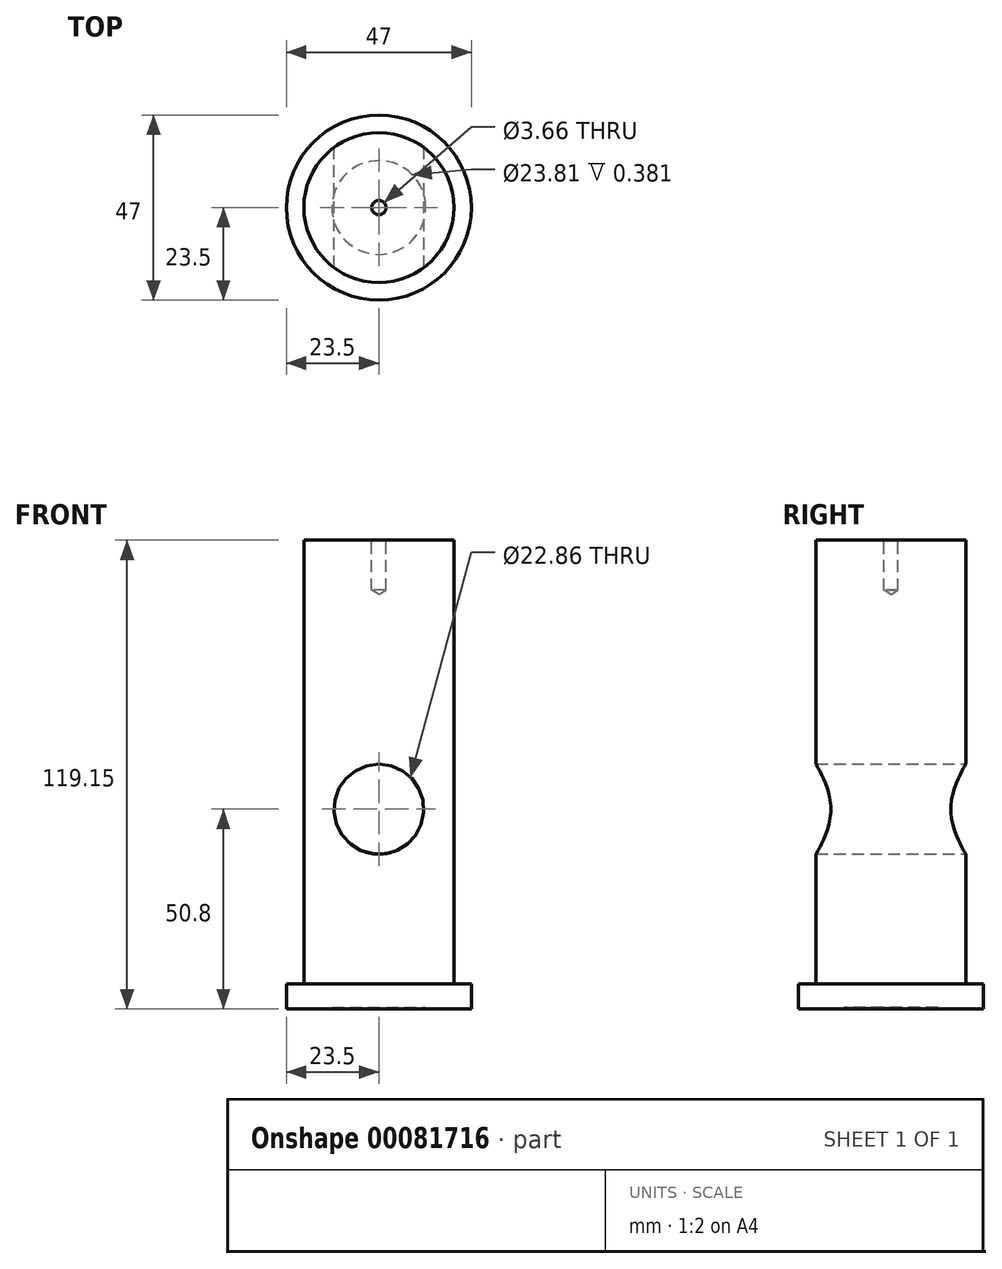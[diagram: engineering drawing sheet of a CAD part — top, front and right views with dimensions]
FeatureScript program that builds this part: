
annotation { "Feature Type Name" : "Feature", "Feature Type Description" : "" }
export const myFeature = defineFeature(function(context is Context, id is Id, definition is map)
    precondition{}
    {
        {
            var Q0;
            Q0=qCreatedBy(makeId("Top.planeOp"),FACE);
            var sketch = newSketch(context, id + "F0", { "sketchPlane" : qUnion([Q0])});
            skCircle(sketch, "E0", {"center": v(0, 0) * mm, "radius": 23.5 * mm});
            skCircle(sketch, "E1", {"center": v(0, 0) * mm, "radius": 19.05 * mm});
            skSolve(sketch);
        }
        {
            var Q0;
            Q0=makeQuery(id+"F0.imprint","IMPRINT",FACE,{"disambiguationData":[TD([[makeQuery(id+"F0.imprint","IMPRINT",EDGE,{"derivedFrom":sQuery(id+"F0.wireOp",EDGE,"E0")}),1.0]])]});
            extrude(context, id + "F1", {"entities" : qUnion([Q0]), "depth" : 6.35 * mm});
        }
        {
            var Q0;
            Q0=makeQuery(id+"F0.imprint","IMPRINT",FACE,{"disambiguationData":[TD([[makeQuery(id+"F0.imprint","IMPRINT",EDGE,{"derivedFrom":sQuery(id+"F0.wireOp",EDGE,"E1")}),1.0]])]});
            extrude(context, id + "F2", {"entities" : qUnion([Q0]), "operationType" : NewBodyOperationType.ADD, "depth" : 119.15 * mm});
        }
        {
            var Q0;
            Q0=makeQuery(id+"F2.opExtrude","CAP_FACE",FACE,{"disambiguationData":[OSD([sQuery(id+"F0.wireOp",EDGE,"E1")])],"isStart":false});
            var sketch = newSketch(context, id + "F3", { "sketchPlane" : qUnion([Q0])});
            skPoint(sketch, "E2", {"position": v(0, 0) * mm});
            skSolve(sketch);
        }
        {
            var Q0;
            Q0=sQuery(id+"F3.wireOp",VERTEX,"E2");
            var Q1;
            Q1=makeQuery(id+"F1.opExtrude","SWEPT_BODY",BODY,{"disambiguationData":[OSD([sQuery(id+"F0.wireOp",EDGE,"E0"),sQuery(id+"F0.wireOp",EDGE,"E1")])]});
            hole(context, id + "F4", {"style" : HoleStyle.SIMPLE, "endStyle" : HoleEndStyle.BLIND, "standardTappedOrClearance" : lookupTablePath({ "standard" : "ANSI", "engagement" : "50%", "pitch" : "32 tpi", "size" : "#8", "type" : "Tapped" }), "standardBlindInLast" : lookupTablePath({ "standard" : "ANSI", "engagement" : "50%", "pitch" : "32 tpi", "size" : "#8", "type" : "Tapped" }), "holeDiameter" : 3.66 * mm, "holeDepth" : 12.7 * mm, "locations" : qUnion([Q0]), "scope" : qUnion([Q1]), "majorDiameter" : 4.17 * mm});
        }
        {
            var Q0;
            Q0=qCreatedBy(makeId("Front.planeOp"),FACE);
            var sketch = newSketch(context, id + "F5", { "sketchPlane" : qUnion([Q0])});
            skCircle(sketch, "E3", {"center": v(0, 50.8) * mm, "radius": 11.43 * mm});
            skSolve(sketch);
        }
        {
            var Q0;
            Q0 = qSketchRegion(id + "F5", true);
            extrude(context, id + "F6", {"entities" : qUnion([Q0]), "operationType" : NewBodyOperationType.REMOVE, "endBound" : BoundingType.SYMMETRIC, "depth" : 50.8 * mm});
        }
        {
            var Q0;
            {var subQ0=sQuery(id+"F0.wireOp",EDGE,"E1");Q0=makeQuery(id+"F2.boolean.opBoolean","MERGE",FACE,{"derivedFrom":[makeQuery(id+"F1.opExtrude","CAP_FACE",FACE,{"disambiguationData":[OSD([sQuery(id+"F0.wireOp",EDGE,"E0"),subQ0])],"isStart":true}),makeQuery(id+"F2.opExtrude","CAP_FACE",FACE,{"disambiguationData":[OSD([subQ0])],"isStart":true})]});}
            var sketch = newSketch(context, id + "F7", { "sketchPlane" : qUnion([Q0])});
            skCircle(sketch, "E4", {"center": v(0, 0) * mm, "radius": 11.9 * mm});
            skSolve(sketch);
        }
        {
            var Q0;
            Q0 = qSketchRegion(id + "F7", true);
            extrude(context, id + "F8", {"entities" : qUnion([Q0]), "operationType" : NewBodyOperationType.REMOVE, "oppositeDirection" : true, "depth" : 0.38 * mm});
        }
    });
